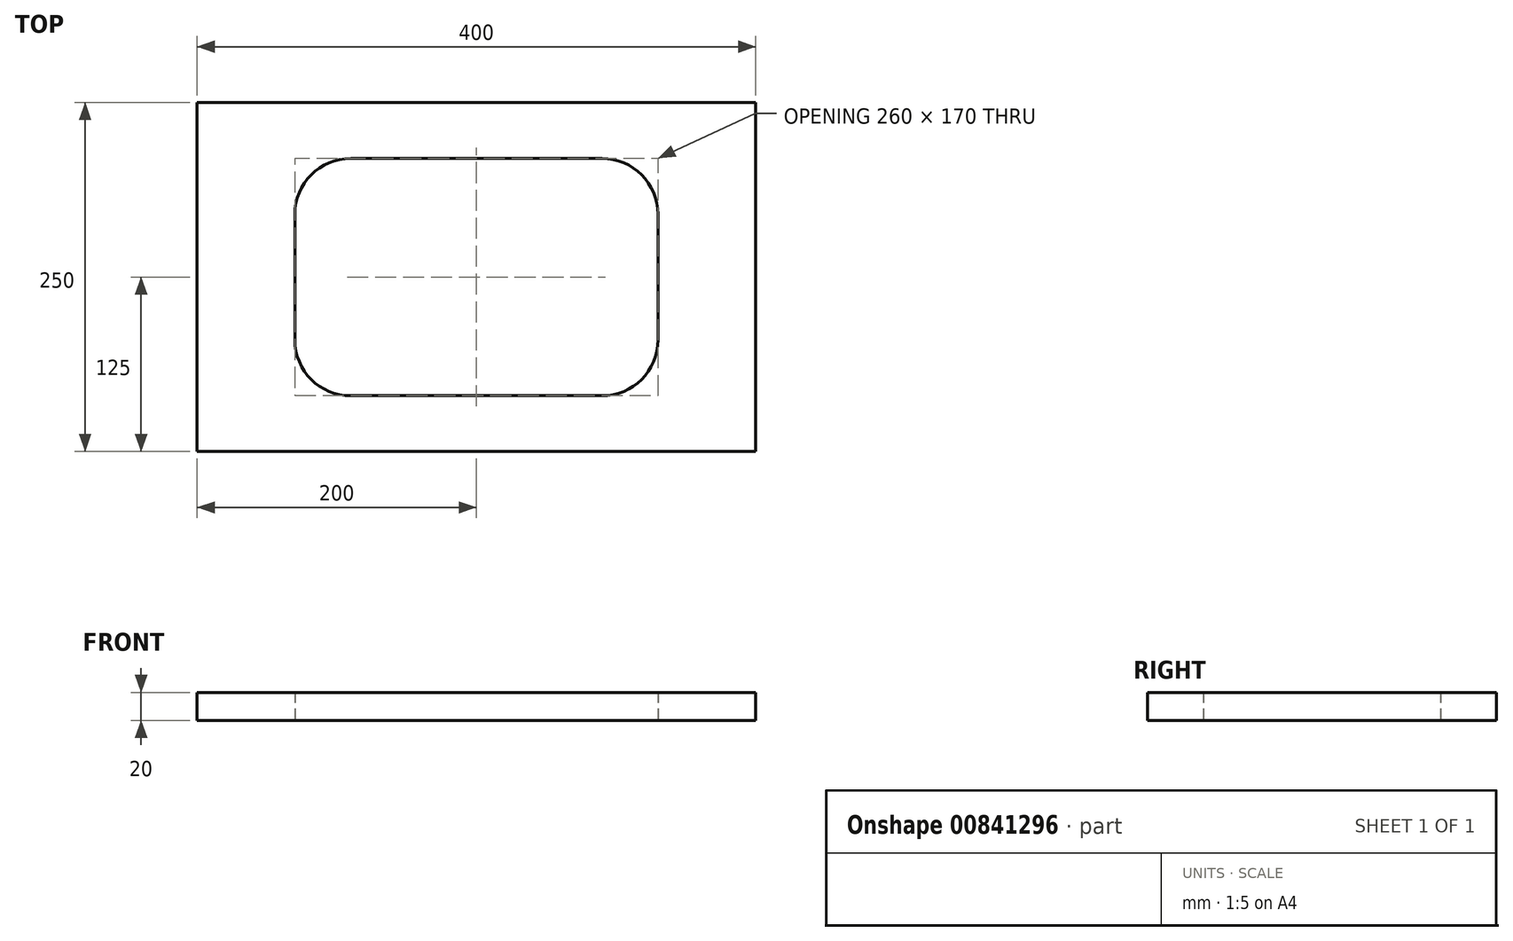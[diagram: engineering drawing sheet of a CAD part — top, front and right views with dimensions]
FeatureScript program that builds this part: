
annotation { "Feature Type Name" : "Feature", "Feature Type Description" : "" }
export const myFeature = defineFeature(function(context is Context, id is Id, definition is map)
    precondition{}
    {
        {
            var Q0;
            Q0=qCreatedBy(makeId("Top.planeOp"),FACE);
            var sketch = newSketch(context, id + "F0", { "sketchPlane" : qUnion([Q0])});
            skLineSegment(sketch, "E0.bottom", {"start": v(200, 125) * mm, "end": v(-200, 125) * mm});
            skLineSegment(sketch, "E0.top", {"start": v(200, -125) * mm, "end": v(-200, -125) * mm});
            skLineSegment(sketch, "E0.left", {"start": v(200, 125) * mm, "end": v(200, -125) * mm});
            skLineSegment(sketch, "E0.right", {"start": v(-200, 125) * mm, "end": v(-200, -125) * mm});
            skPoint(sketch, "E0.middle", {"position": v(0, 0) * mm});
            skLineSegment(sketch, "E1.0", {"start": v(-130, 45) * mm, "end": v(-130, -45) * mm});
            skLineSegment(sketch, "E1.1", {"start": v(90, 85) * mm, "end": v(-90, 85) * mm});
            skLineSegment(sketch, "E1.2", {"start": v(130, 45) * mm, "end": v(130, -45) * mm});
            skLineSegment(sketch, "E1.3", {"start": v(90, -85) * mm, "end": v(-90, -85) * mm});
            skPoint(sketch, "E2.visualSharp", {"position": v(-130, 85) * mm});
            skArc(sketch, "E2.filletArc", {"start": v(-90, 85) * mm, "mid": v(-118.28, 73.28) * mm, "end": v(-130, 45) * mm});
            skPoint(sketch, "E3.visualSharp", {"position": v(-130, -85) * mm});
            skArc(sketch, "E3.filletArc", {"start": v(-130, -45) * mm, "mid": v(-118.28, -73.28) * mm, "end": v(-90, -85) * mm});
            skPoint(sketch, "E4.visualSharp", {"position": v(130, -85) * mm});
            skArc(sketch, "E4.filletArc", {"start": v(90, -85) * mm, "mid": v(118.28, -73.28) * mm, "end": v(130, -45) * mm});
            skPoint(sketch, "E5.visualSharp", {"position": v(130, 85) * mm});
            skArc(sketch, "E5.filletArc", {"start": v(130, 45) * mm, "mid": v(118.28, 73.28) * mm, "end": v(90, 85) * mm});
            skSolve(sketch);
        }
        {
            var Q0;
            Q0=makeQuery(id+"F0.imprint","IMPRINT",FACE,{"disambiguationData":[TD([[makeQuery(id+"F0.imprint","IMPRINT",EDGE,{"derivedFrom":sQuery(id+"F0.wireOp",EDGE,"E0.bottom")}),1.0]])]});
            extrude(context, id + "F1", {"entities" : qUnion([Q0]), "depth" : 20 * mm, "offsetDistance" : 25 * mm});
        }
    });
